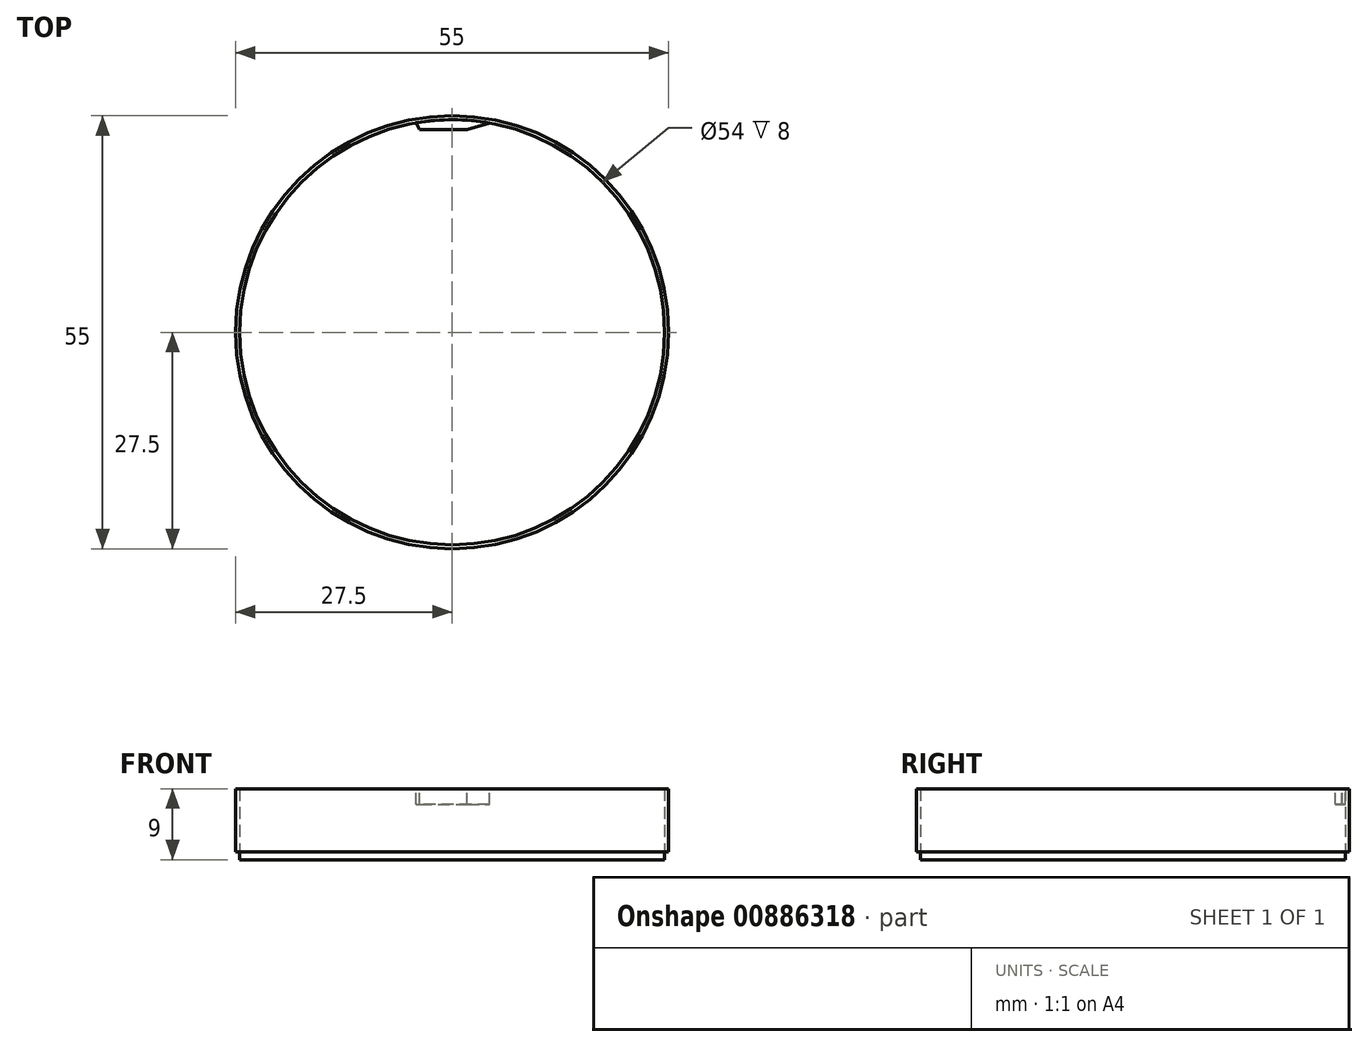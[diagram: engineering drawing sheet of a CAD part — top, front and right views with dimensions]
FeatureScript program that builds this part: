
annotation { "Feature Type Name" : "Feature", "Feature Type Description" : "" }
export const myFeature = defineFeature(function(context is Context, id is Id, definition is map)
    precondition{}
    {
        {
            var Q0;
            Q0=qCreatedBy(makeId("Top.planeOp"),FACE);
            var sketch = newSketch(context, id + "F0", { "sketchPlane" : qUnion([Q0])});
            skCircle(sketch, "E0", {"center": v(0, 0) * mm, "radius": 27.5 * mm});
            skCircle(sketch, "E1", {"center": v(0, 0) * mm, "radius": 27 * mm});
            skSolve(sketch);
        }
        {
            var Q0;
            Q0=makeQuery(id+"F0.imprint","IMPRINT",FACE,{"disambiguationData":[TD([[makeQuery(id+"F0.imprint","IMPRINT",EDGE,{"derivedFrom":sQuery(id+"F0.wireOp",EDGE,"E0")}),1.0]])]});
            extrude(context, id + "F1", {"entities" : qUnion([Q0]), "depth" : 8 * mm, "offsetDistance" : 25 * mm});
        }
        {
            var Q0;
            Q0=makeQuery(id+"F0.imprint","IMPRINT",FACE,{"disambiguationData":[TD([[makeQuery(id+"F0.imprint","IMPRINT",EDGE,{"derivedFrom":sQuery(id+"F0.wireOp",EDGE,"E1")}),1.0]])]});
            extrude(context, id + "F2", {"entities" : qUnion([Q0]), "oppositeDirection" : true, "depth" : 1 * mm, "offsetDistance" : 25 * mm});
        }
        {
            var Q0;
            Q0=makeQuery(id+"F1.opExtrude","CAP_FACE",FACE,{"disambiguationData":[OSD([sQuery(id+"F0.wireOp",EDGE,"E0"),sQuery(id+"F0.wireOp",EDGE,"E1")])],"isStart":false});
            var sketch = newSketch(context, id + "F3", { "sketchPlane" : qUnion([Q0])});
            skLineSegment(sketch, "E2", {"start": v(-4.55, 26.61) * mm, "end": v(-4.1, 25.72) * mm});
            skLineSegment(sketch, "E3", {"start": v(-4.1, 25.72) * mm, "end": v(1.9, 25.72) * mm});
            skLineSegment(sketch, "E4", {"start": v(1.9, 25.72) * mm, "end": v(4.77, 26.58) * mm});
            skSolve(sketch);
        }
        {
            var Q0;
            {var subQ0=sQuery(id+"F3.wireOp",EDGE,"E2");Q0=makeQuery(id+"F3.imprint","IMPRINT",FACE,{"disambiguationData":[TD([[makeQuery(id+"F3.imprint","IMPRINT",EDGE,{"derivedFrom":subQ0}),1.0]])]});}
            extrude(context, id + "F4", {"entities" : qUnion([Q0]), "oppositeDirection" : true, "depth" : 2 * mm, "offsetDistance" : 25 * mm});
        }
    });
